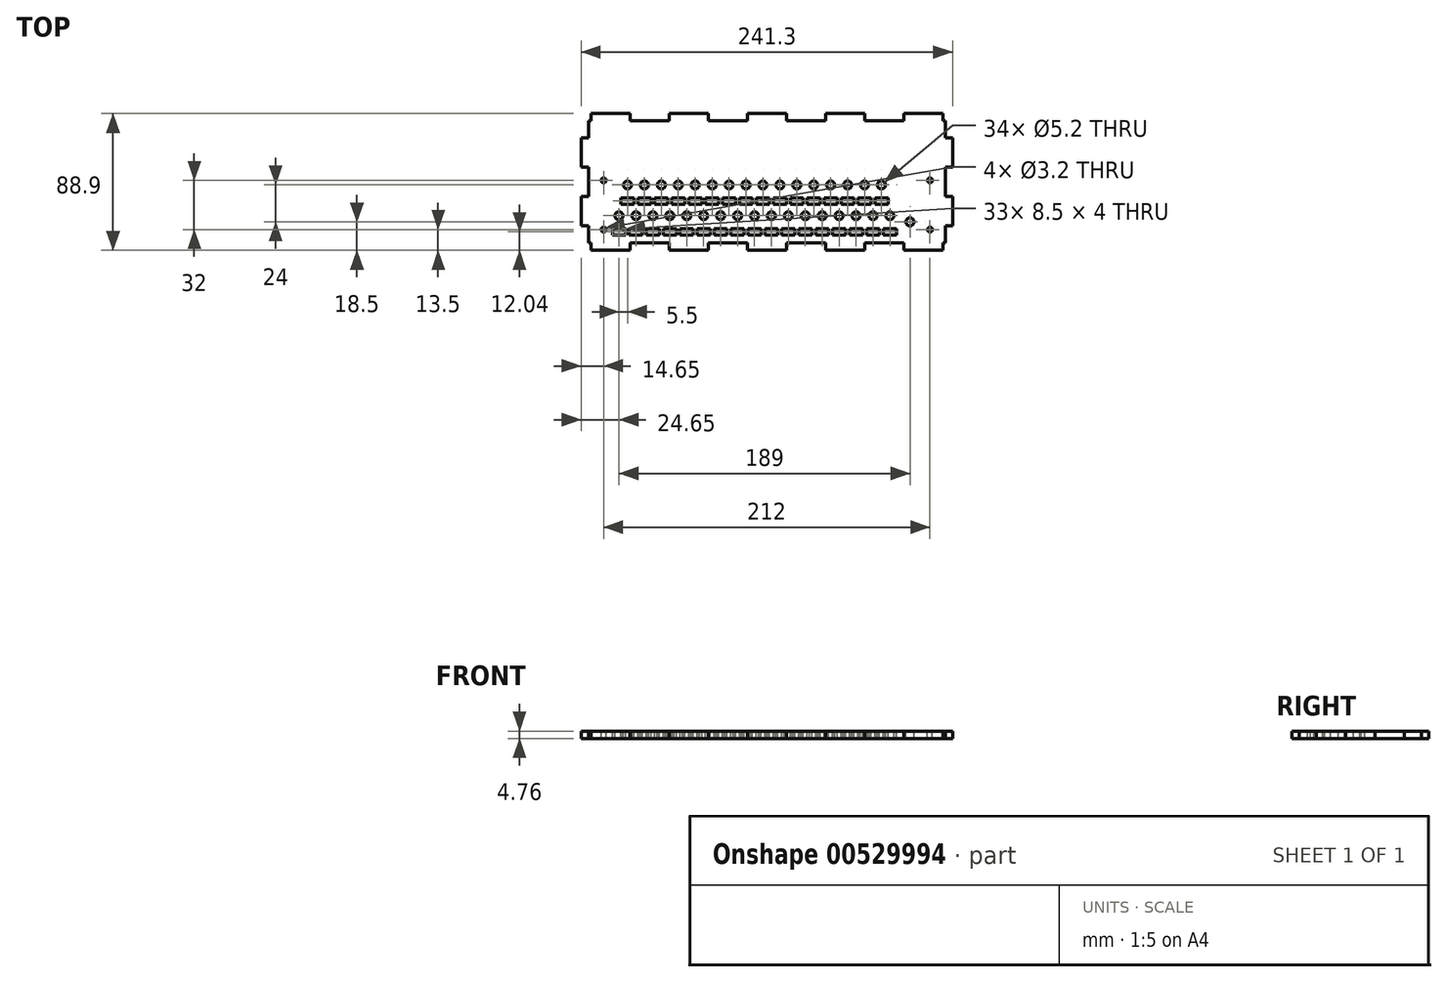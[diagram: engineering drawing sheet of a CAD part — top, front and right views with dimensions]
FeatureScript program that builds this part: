
annotation { "Feature Type Name" : "Feature", "Feature Type Description" : "" }
export const myFeature = defineFeature(function(context is Context, id is Id, definition is map)
    precondition{}
    {
        {
            var Q0;
            Q0=qCreatedBy(makeId("Top.planeOp"),FACE);
            var sketch = newSketch(context, id + "F0", { "sketchPlane" : qUnion([Q0])});
            skLineSegment(sketch, "E0.bottom", {"start": v(-120.65, 44.45) * mm, "end": v(120.65, 44.45) * mm});
            skLineSegment(sketch, "E0.top", {"start": v(-120.65, -44.45) * mm, "end": v(120.65, -44.45) * mm});
            skLineSegment(sketch, "E0.left", {"start": v(-120.65, 44.45) * mm, "end": v(-120.65, -44.45) * mm});
            skLineSegment(sketch, "E0.right", {"start": v(120.65, 44.45) * mm, "end": v(120.65, -44.45) * mm});
            skPoint(sketch, "E0.middle", {"position": v(0, 0) * mm});
            skSolve(sketch);
        }
        {
            var Q0;
            Q0 = qSketchRegion(id + "F0", true);
            extrude(context, id + "F1", {"entities" : qUnion([Q0]), "depth" : 4.76 * mm, "offsetDistance" : 25.4 * mm});
        }
        {
            var Q0;
            Q0=makeQuery(id+"F1.opExtrude","CAP_FACE",FACE,{"disambiguationData":[OSD([sQuery(id+"F0.wireOp",EDGE,"E0.bottom"),sQuery(id+"F0.wireOp",EDGE,"E0.top"),sQuery(id+"F0.wireOp",EDGE,"E0.left"),sQuery(id+"F0.wireOp",EDGE,"E0.right")])],"isStart":false});
            var sketch = newSketch(context, id + "F2", { "sketchPlane" : qUnion([Q0])});
            skLineSegment(sketch, "E1", {"start": v(0, 0) * mm, "end": v(0, -44.45) * mm, "construction": true});
            skLineSegment(sketch, "E2", {"start": v(-110, 44.45) * mm, "end": v(-110, -44.45) * mm, "construction": true});
            skCircle(sketch, "E3", {"center": v(-96, -21.95) * mm, "radius": 2.6 * mm});
            skCircle(sketch, "E4.1.0.0", {"center": v(-85, -21.95) * mm, "radius": 2.6 * mm});
            skCircle(sketch, "E4.2.0.0", {"center": v(-74, -21.95) * mm, "radius": 2.6 * mm});
            skCircle(sketch, "E4.3.0.0", {"center": v(-63, -21.95) * mm, "radius": 2.6 * mm});
            skCircle(sketch, "E4.4.0.0", {"center": v(-52, -21.95) * mm, "radius": 2.6 * mm});
            skCircle(sketch, "E4.5.0.0", {"center": v(-41, -21.95) * mm, "radius": 2.6 * mm});
            skCircle(sketch, "E4.6.0.0", {"center": v(-30, -21.95) * mm, "radius": 2.6 * mm});
            skCircle(sketch, "E4.7.0.0", {"center": v(-19, -21.95) * mm, "radius": 2.6 * mm});
            skCircle(sketch, "E4.8.0.0", {"center": v(-8, -21.95) * mm, "radius": 2.6 * mm});
            skCircle(sketch, "E4.9.0.0", {"center": v(3, -21.95) * mm, "radius": 2.6 * mm});
            skCircle(sketch, "E4.10.0.0", {"center": v(14, -21.95) * mm, "radius": 2.6 * mm});
            skCircle(sketch, "E4.11.0.0", {"center": v(25, -21.95) * mm, "radius": 2.6 * mm});
            skCircle(sketch, "E4.12.0.0", {"center": v(36, -21.95) * mm, "radius": 2.6 * mm});
            skCircle(sketch, "E4.13.0.0", {"center": v(47, -21.95) * mm, "radius": 2.6 * mm});
            skCircle(sketch, "E4.14.0.0", {"center": v(58, -21.95) * mm, "radius": 2.6 * mm});
            skCircle(sketch, "E4.15.0.0", {"center": v(69, -21.95) * mm, "radius": 2.6 * mm});
            skCircle(sketch, "E4.16.0.0", {"center": v(80, -21.95) * mm, "radius": 2.6 * mm});
            skLineSegment(sketch, "E4.direction1", {"start": v(-96, -21.95) * mm, "end": v(-85, -21.95) * mm, "construction": true});
            skCircle(sketch, "E5", {"center": v(93, -25.95) * mm, "radius": 2.6 * mm});
            skCircle(sketch, "E6", {"center": v(-90.5, -1.95) * mm, "radius": 2.6 * mm});
            skCircle(sketch, "E7.1.0.0", {"center": v(-79.5, -1.95) * mm, "radius": 2.6 * mm});
            skCircle(sketch, "E7.2.0.0", {"center": v(-68.5, -1.95) * mm, "radius": 2.6 * mm});
            skCircle(sketch, "E7.3.0.0", {"center": v(-57.5, -1.95) * mm, "radius": 2.6 * mm});
            skCircle(sketch, "E7.4.0.0", {"center": v(-46.5, -1.95) * mm, "radius": 2.6 * mm});
            skCircle(sketch, "E7.5.0.0", {"center": v(-35.5, -1.95) * mm, "radius": 2.6 * mm});
            skCircle(sketch, "E7.6.0.0", {"center": v(-24.5, -1.95) * mm, "radius": 2.6 * mm});
            skCircle(sketch, "E7.7.0.0", {"center": v(-13.5, -1.95) * mm, "radius": 2.6 * mm});
            skCircle(sketch, "E7.8.0.0", {"center": v(-2.5, -1.95) * mm, "radius": 2.6 * mm});
            skCircle(sketch, "E7.9.0.0", {"center": v(8.5, -1.95) * mm, "radius": 2.6 * mm});
            skCircle(sketch, "E7.10.0.0", {"center": v(19.5, -1.95) * mm, "radius": 2.6 * mm});
            skCircle(sketch, "E7.11.0.0", {"center": v(30.5, -1.95) * mm, "radius": 2.6 * mm});
            skCircle(sketch, "E7.12.0.0", {"center": v(41.5, -1.95) * mm, "radius": 2.6 * mm});
            skCircle(sketch, "E7.13.0.0", {"center": v(52.5, -1.95) * mm, "radius": 2.6 * mm});
            skCircle(sketch, "E7.14.0.0", {"center": v(63.5, -1.95) * mm, "radius": 2.6 * mm});
            skCircle(sketch, "E7.15.0.0", {"center": v(74.5, -1.95) * mm, "radius": 2.6 * mm});
            skLineSegment(sketch, "E7.direction1", {"start": v(-90.5, -1.95) * mm, "end": v(-79.5, -1.95) * mm, "construction": true});
            skSolve(sketch);
        }
        {
            var Q0;
            Q0 = qSketchRegion(id + "F2", true);
            extrude(context, id + "F3", {"entities" : qUnion([Q0]), "operationType" : NewBodyOperationType.REMOVE, "oppositeDirection" : true, "depth" : 25.4 * mm, "offsetDistance" : 25.4 * mm});
        }
        {
            var Q0;
            Q0=makeQuery(id+"F1.opExtrude","CAP_FACE",FACE,{"disambiguationData":[OSD([sQuery(id+"F0.wireOp",EDGE,"E0.bottom"),sQuery(id+"F0.wireOp",EDGE,"E0.top"),sQuery(id+"F0.wireOp",EDGE,"E0.left"),sQuery(id+"F0.wireOp",EDGE,"E0.right")])],"isStart":false});
            var sketch = newSketch(context, id + "F4", { "sketchPlane" : qUnion([Q0])});
            skLineSegment(sketch, "E8.bottom", {"start": v(-94.75, -10.41) * mm, "end": v(-86.25, -10.41) * mm});
            skLineSegment(sketch, "E8.top", {"start": v(-94.75, -14.41) * mm, "end": v(-86.25, -14.41) * mm});
            skLineSegment(sketch, "E8.left", {"start": v(-94.75, -10.41) * mm, "end": v(-94.75, -14.41) * mm});
            skLineSegment(sketch, "E8.right", {"start": v(-86.25, -10.41) * mm, "end": v(-86.25, -14.41) * mm});
            skLineSegment(sketch, "E9", {"start": v(-90.5, -10.41) * mm, "end": v(-90.5, -14.41) * mm, "construction": true});
            skLineSegment(sketch, "E10", {"start": v(-94.75, -12.41) * mm, "end": v(-90.5, -12.41) * mm, "construction": true});
            skLineSegment(sketch, "E11", {"start": v(-90.5, -1.95) * mm, "end": v(-90.5, -9.77) * mm, "construction": true});
            skLineSegment(sketch, "E12.1.0.0", {"start": v(-79.5, -10.41) * mm, "end": v(-79.5, -14.41) * mm, "construction": true});
            skLineSegment(sketch, "E12.1.0.1", {"start": v(-83.75, -10.41) * mm, "end": v(-75.25, -10.41) * mm});
            skLineSegment(sketch, "E12.1.0.2", {"start": v(-83.75, -10.41) * mm, "end": v(-83.75, -14.41) * mm});
            skLineSegment(sketch, "E12.1.0.3", {"start": v(-83.75, -14.41) * mm, "end": v(-75.25, -14.41) * mm});
            skLineSegment(sketch, "E12.1.0.4", {"start": v(-75.25, -10.41) * mm, "end": v(-75.25, -14.41) * mm});
            skLineSegment(sketch, "E12.2.0.0", {"start": v(-68.5, -10.41) * mm, "end": v(-68.5, -14.41) * mm, "construction": true});
            skLineSegment(sketch, "E12.2.0.1", {"start": v(-72.75, -10.41) * mm, "end": v(-64.25, -10.41) * mm});
            skLineSegment(sketch, "E12.2.0.2", {"start": v(-72.75, -10.41) * mm, "end": v(-72.75, -14.41) * mm});
            skLineSegment(sketch, "E12.2.0.3", {"start": v(-72.75, -14.41) * mm, "end": v(-64.25, -14.41) * mm});
            skLineSegment(sketch, "E12.2.0.4", {"start": v(-64.25, -10.41) * mm, "end": v(-64.25, -14.41) * mm});
            skLineSegment(sketch, "E12.3.0.0", {"start": v(-57.5, -10.41) * mm, "end": v(-57.5, -14.41) * mm, "construction": true});
            skLineSegment(sketch, "E12.3.0.1", {"start": v(-61.75, -10.41) * mm, "end": v(-53.25, -10.41) * mm});
            skLineSegment(sketch, "E12.3.0.2", {"start": v(-61.75, -10.41) * mm, "end": v(-61.75, -14.41) * mm});
            skLineSegment(sketch, "E12.3.0.3", {"start": v(-61.75, -14.41) * mm, "end": v(-53.25, -14.41) * mm});
            skLineSegment(sketch, "E12.3.0.4", {"start": v(-53.25, -10.41) * mm, "end": v(-53.25, -14.41) * mm});
            skLineSegment(sketch, "E12.4.0.0", {"start": v(-46.5, -10.41) * mm, "end": v(-46.5, -14.41) * mm, "construction": true});
            skLineSegment(sketch, "E12.4.0.1", {"start": v(-50.75, -10.41) * mm, "end": v(-42.25, -10.41) * mm});
            skLineSegment(sketch, "E12.4.0.2", {"start": v(-50.75, -10.41) * mm, "end": v(-50.75, -14.41) * mm});
            skLineSegment(sketch, "E12.4.0.3", {"start": v(-50.75, -14.41) * mm, "end": v(-42.25, -14.41) * mm});
            skLineSegment(sketch, "E12.4.0.4", {"start": v(-42.25, -10.41) * mm, "end": v(-42.25, -14.41) * mm});
            skLineSegment(sketch, "E12.5.0.0", {"start": v(-35.5, -10.41) * mm, "end": v(-35.5, -14.41) * mm, "construction": true});
            skLineSegment(sketch, "E12.5.0.1", {"start": v(-39.75, -10.41) * mm, "end": v(-31.25, -10.41) * mm});
            skLineSegment(sketch, "E12.5.0.2", {"start": v(-39.75, -10.41) * mm, "end": v(-39.75, -14.41) * mm});
            skLineSegment(sketch, "E12.5.0.3", {"start": v(-39.75, -14.41) * mm, "end": v(-31.25, -14.41) * mm});
            skLineSegment(sketch, "E12.5.0.4", {"start": v(-31.25, -10.41) * mm, "end": v(-31.25, -14.41) * mm});
            skLineSegment(sketch, "E12.6.0.0", {"start": v(-24.5, -10.41) * mm, "end": v(-24.5, -14.41) * mm, "construction": true});
            skLineSegment(sketch, "E12.6.0.1", {"start": v(-28.75, -10.41) * mm, "end": v(-20.25, -10.41) * mm});
            skLineSegment(sketch, "E12.6.0.2", {"start": v(-28.75, -10.41) * mm, "end": v(-28.75, -14.41) * mm});
            skLineSegment(sketch, "E12.6.0.3", {"start": v(-28.75, -14.41) * mm, "end": v(-20.25, -14.41) * mm});
            skLineSegment(sketch, "E12.6.0.4", {"start": v(-20.25, -10.41) * mm, "end": v(-20.25, -14.41) * mm});
            skLineSegment(sketch, "E12.7.0.0", {"start": v(-13.5, -10.41) * mm, "end": v(-13.5, -14.41) * mm, "construction": true});
            skLineSegment(sketch, "E12.7.0.1", {"start": v(-17.75, -10.41) * mm, "end": v(-9.25, -10.41) * mm});
            skLineSegment(sketch, "E12.7.0.2", {"start": v(-17.75, -10.41) * mm, "end": v(-17.75, -14.41) * mm});
            skLineSegment(sketch, "E12.7.0.3", {"start": v(-17.75, -14.41) * mm, "end": v(-9.25, -14.41) * mm});
            skLineSegment(sketch, "E12.7.0.4", {"start": v(-9.25, -10.41) * mm, "end": v(-9.25, -14.41) * mm});
            skLineSegment(sketch, "E12.8.0.0", {"start": v(-2.5, -10.41) * mm, "end": v(-2.5, -14.41) * mm, "construction": true});
            skLineSegment(sketch, "E12.8.0.1", {"start": v(-6.75, -10.41) * mm, "end": v(1.75, -10.41) * mm});
            skLineSegment(sketch, "E12.8.0.2", {"start": v(-6.75, -10.41) * mm, "end": v(-6.75, -14.41) * mm});
            skLineSegment(sketch, "E12.8.0.3", {"start": v(-6.75, -14.41) * mm, "end": v(1.75, -14.41) * mm});
            skLineSegment(sketch, "E12.8.0.4", {"start": v(1.75, -10.41) * mm, "end": v(1.75, -14.41) * mm});
            skLineSegment(sketch, "E12.9.0.0", {"start": v(8.5, -10.41) * mm, "end": v(8.5, -14.41) * mm, "construction": true});
            skLineSegment(sketch, "E12.9.0.1", {"start": v(4.25, -10.41) * mm, "end": v(12.75, -10.41) * mm});
            skLineSegment(sketch, "E12.9.0.2", {"start": v(4.25, -10.41) * mm, "end": v(4.25, -14.41) * mm});
            skLineSegment(sketch, "E12.9.0.3", {"start": v(4.25, -14.41) * mm, "end": v(12.75, -14.41) * mm});
            skLineSegment(sketch, "E12.9.0.4", {"start": v(12.75, -10.41) * mm, "end": v(12.75, -14.41) * mm});
            skLineSegment(sketch, "E12.10.0.0", {"start": v(19.5, -10.41) * mm, "end": v(19.5, -14.41) * mm, "construction": true});
            skLineSegment(sketch, "E12.10.0.1", {"start": v(15.25, -10.41) * mm, "end": v(23.75, -10.41) * mm});
            skLineSegment(sketch, "E12.10.0.2", {"start": v(15.25, -10.41) * mm, "end": v(15.25, -14.41) * mm});
            skLineSegment(sketch, "E12.10.0.3", {"start": v(15.25, -14.41) * mm, "end": v(23.75, -14.41) * mm});
            skLineSegment(sketch, "E12.10.0.4", {"start": v(23.75, -10.41) * mm, "end": v(23.75, -14.41) * mm});
            skLineSegment(sketch, "E12.11.0.0", {"start": v(30.5, -10.41) * mm, "end": v(30.5, -14.41) * mm, "construction": true});
            skLineSegment(sketch, "E12.11.0.1", {"start": v(26.25, -10.41) * mm, "end": v(34.75, -10.41) * mm});
            skLineSegment(sketch, "E12.11.0.2", {"start": v(26.25, -10.41) * mm, "end": v(26.25, -14.41) * mm});
            skLineSegment(sketch, "E12.11.0.3", {"start": v(26.25, -14.41) * mm, "end": v(34.75, -14.41) * mm});
            skLineSegment(sketch, "E12.11.0.4", {"start": v(34.75, -10.41) * mm, "end": v(34.75, -14.41) * mm});
            skLineSegment(sketch, "E12.12.0.0", {"start": v(41.5, -10.41) * mm, "end": v(41.5, -14.41) * mm, "construction": true});
            skLineSegment(sketch, "E12.12.0.1", {"start": v(37.25, -10.41) * mm, "end": v(45.75, -10.41) * mm});
            skLineSegment(sketch, "E12.12.0.2", {"start": v(37.25, -10.41) * mm, "end": v(37.25, -14.41) * mm});
            skLineSegment(sketch, "E12.12.0.3", {"start": v(37.25, -14.41) * mm, "end": v(45.75, -14.41) * mm});
            skLineSegment(sketch, "E12.12.0.4", {"start": v(45.75, -10.41) * mm, "end": v(45.75, -14.41) * mm});
            skLineSegment(sketch, "E12.13.0.0", {"start": v(52.5, -10.41) * mm, "end": v(52.5, -14.41) * mm, "construction": true});
            skLineSegment(sketch, "E12.13.0.1", {"start": v(48.25, -10.41) * mm, "end": v(56.75, -10.41) * mm});
            skLineSegment(sketch, "E12.13.0.2", {"start": v(48.25, -10.41) * mm, "end": v(48.25, -14.41) * mm});
            skLineSegment(sketch, "E12.13.0.3", {"start": v(48.25, -14.41) * mm, "end": v(56.75, -14.41) * mm});
            skLineSegment(sketch, "E12.13.0.4", {"start": v(56.75, -10.41) * mm, "end": v(56.75, -14.41) * mm});
            skLineSegment(sketch, "E12.14.0.0", {"start": v(63.5, -10.41) * mm, "end": v(63.5, -14.41) * mm, "construction": true});
            skLineSegment(sketch, "E12.14.0.1", {"start": v(59.25, -10.41) * mm, "end": v(67.75, -10.41) * mm});
            skLineSegment(sketch, "E12.14.0.2", {"start": v(59.25, -10.41) * mm, "end": v(59.25, -14.41) * mm});
            skLineSegment(sketch, "E12.14.0.3", {"start": v(59.25, -14.41) * mm, "end": v(67.75, -14.41) * mm});
            skLineSegment(sketch, "E12.14.0.4", {"start": v(67.75, -10.41) * mm, "end": v(67.75, -14.41) * mm});
            skLineSegment(sketch, "E12.15.0.0", {"start": v(74.5, -10.41) * mm, "end": v(74.5, -14.41) * mm, "construction": true});
            skLineSegment(sketch, "E12.15.0.1", {"start": v(70.25, -10.41) * mm, "end": v(78.75, -10.41) * mm});
            skLineSegment(sketch, "E12.15.0.2", {"start": v(70.25, -10.41) * mm, "end": v(70.25, -14.41) * mm});
            skLineSegment(sketch, "E12.15.0.3", {"start": v(70.25, -14.41) * mm, "end": v(78.75, -14.41) * mm});
            skLineSegment(sketch, "E12.15.0.4", {"start": v(78.75, -10.41) * mm, "end": v(78.75, -14.41) * mm});
            skLineSegment(sketch, "E12.direction1", {"start": v(-90.5, -14.41) * mm, "end": v(-79.5, -14.41) * mm, "construction": true});
            skLineSegment(sketch, "E13.bottom", {"start": v(-100.25, -30.41) * mm, "end": v(-91.75, -30.41) * mm});
            skLineSegment(sketch, "E13.top", {"start": v(-100.25, -34.41) * mm, "end": v(-91.75, -34.41) * mm});
            skLineSegment(sketch, "E13.left", {"start": v(-100.25, -30.41) * mm, "end": v(-100.25, -34.41) * mm});
            skLineSegment(sketch, "E13.right", {"start": v(-91.75, -30.41) * mm, "end": v(-91.75, -34.41) * mm});
            skLineSegment(sketch, "E14", {"start": v(-96, -30.4) * mm, "end": v(-96, -34.41) * mm, "construction": true});
            skLineSegment(sketch, "E15", {"start": v(-96, -34.41) * mm, "end": v(-96, -32.41) * mm, "construction": true});
            skLineSegment(sketch, "E16", {"start": v(-96, -32.41) * mm, "end": v(-100.25, -32.41) * mm, "construction": true});
            skLineSegment(sketch, "E17", {"start": v(-96, -21.95) * mm, "end": v(-96, -29.83) * mm, "construction": true});
            skLineSegment(sketch, "E18.1.0.0", {"start": v(-85, -34.41) * mm, "end": v(-85, -32.41) * mm, "construction": true});
            skLineSegment(sketch, "E18.1.0.1", {"start": v(-89.25, -30.41) * mm, "end": v(-89.25, -34.41) * mm});
            skLineSegment(sketch, "E18.1.0.2", {"start": v(-89.25, -30.41) * mm, "end": v(-80.75, -30.41) * mm});
            skLineSegment(sketch, "E18.1.0.3", {"start": v(-89.25, -34.41) * mm, "end": v(-80.75, -34.41) * mm});
            skLineSegment(sketch, "E18.1.0.4", {"start": v(-80.75, -30.41) * mm, "end": v(-80.75, -34.41) * mm});
            skLineSegment(sketch, "E18.2.0.0", {"start": v(-74, -34.41) * mm, "end": v(-74, -32.41) * mm, "construction": true});
            skLineSegment(sketch, "E18.2.0.1", {"start": v(-78.25, -30.41) * mm, "end": v(-78.25, -34.41) * mm});
            skLineSegment(sketch, "E18.2.0.2", {"start": v(-78.25, -30.41) * mm, "end": v(-69.75, -30.41) * mm});
            skLineSegment(sketch, "E18.2.0.3", {"start": v(-78.25, -34.41) * mm, "end": v(-69.75, -34.41) * mm});
            skLineSegment(sketch, "E18.2.0.4", {"start": v(-69.75, -30.41) * mm, "end": v(-69.75, -34.41) * mm});
            skLineSegment(sketch, "E18.3.0.0", {"start": v(-63, -34.41) * mm, "end": v(-63, -32.41) * mm, "construction": true});
            skLineSegment(sketch, "E18.3.0.1", {"start": v(-67.25, -30.41) * mm, "end": v(-67.25, -34.41) * mm});
            skLineSegment(sketch, "E18.3.0.2", {"start": v(-67.25, -30.41) * mm, "end": v(-58.75, -30.41) * mm});
            skLineSegment(sketch, "E18.3.0.3", {"start": v(-67.25, -34.41) * mm, "end": v(-58.75, -34.41) * mm});
            skLineSegment(sketch, "E18.3.0.4", {"start": v(-58.75, -30.41) * mm, "end": v(-58.75, -34.41) * mm});
            skLineSegment(sketch, "E18.4.0.0", {"start": v(-52, -34.41) * mm, "end": v(-52, -32.41) * mm, "construction": true});
            skLineSegment(sketch, "E18.4.0.1", {"start": v(-56.25, -30.41) * mm, "end": v(-56.25, -34.41) * mm});
            skLineSegment(sketch, "E18.4.0.2", {"start": v(-56.25, -30.41) * mm, "end": v(-47.75, -30.41) * mm});
            skLineSegment(sketch, "E18.4.0.3", {"start": v(-56.25, -34.41) * mm, "end": v(-47.75, -34.41) * mm});
            skLineSegment(sketch, "E18.4.0.4", {"start": v(-47.75, -30.41) * mm, "end": v(-47.75, -34.41) * mm});
            skLineSegment(sketch, "E18.5.0.0", {"start": v(-41, -34.41) * mm, "end": v(-41, -32.41) * mm, "construction": true});
            skLineSegment(sketch, "E18.5.0.1", {"start": v(-45.25, -30.41) * mm, "end": v(-45.25, -34.41) * mm});
            skLineSegment(sketch, "E18.5.0.2", {"start": v(-45.25, -30.41) * mm, "end": v(-36.75, -30.41) * mm});
            skLineSegment(sketch, "E18.5.0.3", {"start": v(-45.25, -34.41) * mm, "end": v(-36.75, -34.41) * mm});
            skLineSegment(sketch, "E18.5.0.4", {"start": v(-36.75, -30.41) * mm, "end": v(-36.75, -34.41) * mm});
            skLineSegment(sketch, "E18.6.0.0", {"start": v(-30, -34.41) * mm, "end": v(-30, -32.41) * mm, "construction": true});
            skLineSegment(sketch, "E18.6.0.1", {"start": v(-34.25, -30.41) * mm, "end": v(-34.25, -34.41) * mm});
            skLineSegment(sketch, "E18.6.0.2", {"start": v(-34.25, -30.41) * mm, "end": v(-25.75, -30.41) * mm});
            skLineSegment(sketch, "E18.6.0.3", {"start": v(-34.25, -34.41) * mm, "end": v(-25.75, -34.41) * mm});
            skLineSegment(sketch, "E18.6.0.4", {"start": v(-25.75, -30.41) * mm, "end": v(-25.75, -34.41) * mm});
            skLineSegment(sketch, "E18.7.0.0", {"start": v(-19, -34.41) * mm, "end": v(-19, -32.41) * mm, "construction": true});
            skLineSegment(sketch, "E18.7.0.1", {"start": v(-23.25, -30.41) * mm, "end": v(-23.25, -34.41) * mm});
            skLineSegment(sketch, "E18.7.0.2", {"start": v(-23.25, -30.41) * mm, "end": v(-14.75, -30.41) * mm});
            skLineSegment(sketch, "E18.7.0.3", {"start": v(-23.25, -34.41) * mm, "end": v(-14.75, -34.41) * mm});
            skLineSegment(sketch, "E18.7.0.4", {"start": v(-14.75, -30.41) * mm, "end": v(-14.75, -34.41) * mm});
            skLineSegment(sketch, "E18.8.0.0", {"start": v(-8, -34.41) * mm, "end": v(-8, -32.41) * mm, "construction": true});
            skLineSegment(sketch, "E18.8.0.1", {"start": v(-12.25, -30.41) * mm, "end": v(-12.25, -34.41) * mm});
            skLineSegment(sketch, "E18.8.0.2", {"start": v(-12.25, -30.41) * mm, "end": v(-3.75, -30.41) * mm});
            skLineSegment(sketch, "E18.8.0.3", {"start": v(-12.25, -34.41) * mm, "end": v(-3.75, -34.41) * mm});
            skLineSegment(sketch, "E18.8.0.4", {"start": v(-3.75, -30.41) * mm, "end": v(-3.75, -34.41) * mm});
            skLineSegment(sketch, "E18.9.0.0", {"start": v(3, -34.41) * mm, "end": v(3, -32.41) * mm, "construction": true});
            skLineSegment(sketch, "E18.9.0.1", {"start": v(-1.25, -30.41) * mm, "end": v(-1.25, -34.41) * mm});
            skLineSegment(sketch, "E18.9.0.2", {"start": v(-1.25, -30.41) * mm, "end": v(7.25, -30.41) * mm});
            skLineSegment(sketch, "E18.9.0.3", {"start": v(-1.25, -34.41) * mm, "end": v(7.25, -34.41) * mm});
            skLineSegment(sketch, "E18.9.0.4", {"start": v(7.25, -30.41) * mm, "end": v(7.25, -34.41) * mm});
            skLineSegment(sketch, "E18.10.0.0", {"start": v(14, -34.41) * mm, "end": v(14, -32.41) * mm, "construction": true});
            skLineSegment(sketch, "E18.10.0.1", {"start": v(9.75, -30.41) * mm, "end": v(9.75, -34.41) * mm});
            skLineSegment(sketch, "E18.10.0.2", {"start": v(9.75, -30.41) * mm, "end": v(18.25, -30.41) * mm});
            skLineSegment(sketch, "E18.10.0.3", {"start": v(9.75, -34.41) * mm, "end": v(18.25, -34.41) * mm});
            skLineSegment(sketch, "E18.10.0.4", {"start": v(18.25, -30.41) * mm, "end": v(18.25, -34.41) * mm});
            skLineSegment(sketch, "E18.11.0.0", {"start": v(25, -34.41) * mm, "end": v(25, -32.41) * mm, "construction": true});
            skLineSegment(sketch, "E18.11.0.1", {"start": v(20.75, -30.41) * mm, "end": v(20.75, -34.41) * mm});
            skLineSegment(sketch, "E18.11.0.2", {"start": v(20.75, -30.41) * mm, "end": v(29.25, -30.41) * mm});
            skLineSegment(sketch, "E18.11.0.3", {"start": v(20.75, -34.41) * mm, "end": v(29.25, -34.41) * mm});
            skLineSegment(sketch, "E18.11.0.4", {"start": v(29.25, -30.41) * mm, "end": v(29.25, -34.41) * mm});
            skLineSegment(sketch, "E18.12.0.0", {"start": v(36, -34.41) * mm, "end": v(36, -32.41) * mm, "construction": true});
            skLineSegment(sketch, "E18.12.0.1", {"start": v(31.75, -30.41) * mm, "end": v(31.75, -34.41) * mm});
            skLineSegment(sketch, "E18.12.0.2", {"start": v(31.75, -30.41) * mm, "end": v(40.25, -30.41) * mm});
            skLineSegment(sketch, "E18.12.0.3", {"start": v(31.75, -34.41) * mm, "end": v(40.25, -34.41) * mm});
            skLineSegment(sketch, "E18.12.0.4", {"start": v(40.25, -30.41) * mm, "end": v(40.25, -34.41) * mm});
            skLineSegment(sketch, "E18.13.0.0", {"start": v(47, -34.41) * mm, "end": v(47, -32.41) * mm, "construction": true});
            skLineSegment(sketch, "E18.13.0.1", {"start": v(42.75, -30.41) * mm, "end": v(42.75, -34.41) * mm});
            skLineSegment(sketch, "E18.13.0.2", {"start": v(42.75, -30.41) * mm, "end": v(51.25, -30.41) * mm});
            skLineSegment(sketch, "E18.13.0.3", {"start": v(42.75, -34.41) * mm, "end": v(51.25, -34.41) * mm});
            skLineSegment(sketch, "E18.13.0.4", {"start": v(51.25, -30.41) * mm, "end": v(51.25, -34.41) * mm});
            skLineSegment(sketch, "E18.14.0.0", {"start": v(58, -34.41) * mm, "end": v(58, -32.41) * mm, "construction": true});
            skLineSegment(sketch, "E18.14.0.1", {"start": v(53.75, -30.41) * mm, "end": v(53.75, -34.41) * mm});
            skLineSegment(sketch, "E18.14.0.2", {"start": v(53.75, -30.41) * mm, "end": v(62.25, -30.41) * mm});
            skLineSegment(sketch, "E18.14.0.3", {"start": v(53.75, -34.41) * mm, "end": v(62.25, -34.41) * mm});
            skLineSegment(sketch, "E18.14.0.4", {"start": v(62.25, -30.41) * mm, "end": v(62.25, -34.41) * mm});
            skLineSegment(sketch, "E18.15.0.0", {"start": v(69, -34.41) * mm, "end": v(69, -32.41) * mm, "construction": true});
            skLineSegment(sketch, "E18.15.0.1", {"start": v(64.75, -30.41) * mm, "end": v(64.75, -34.41) * mm});
            skLineSegment(sketch, "E18.15.0.2", {"start": v(64.75, -30.41) * mm, "end": v(73.25, -30.41) * mm});
            skLineSegment(sketch, "E18.15.0.3", {"start": v(64.75, -34.41) * mm, "end": v(73.25, -34.41) * mm});
            skLineSegment(sketch, "E18.15.0.4", {"start": v(73.25, -30.41) * mm, "end": v(73.25, -34.41) * mm});
            skLineSegment(sketch, "E18.16.0.0", {"start": v(80, -34.41) * mm, "end": v(80, -32.41) * mm, "construction": true});
            skLineSegment(sketch, "E18.16.0.1", {"start": v(75.75, -30.41) * mm, "end": v(75.75, -34.41) * mm});
            skLineSegment(sketch, "E18.16.0.2", {"start": v(75.75, -30.41) * mm, "end": v(84.25, -30.41) * mm});
            skLineSegment(sketch, "E18.16.0.3", {"start": v(75.75, -34.41) * mm, "end": v(84.25, -34.41) * mm});
            skLineSegment(sketch, "E18.16.0.4", {"start": v(84.25, -30.41) * mm, "end": v(84.25, -34.41) * mm});
            skLineSegment(sketch, "E18.direction1", {"start": v(-96, -34.41) * mm, "end": v(-85, -34.41) * mm, "construction": true});
            skSolve(sketch);
        }
        {
            var Q0;
            Q0 = qSketchRegion(id + "F4", true);
            extrude(context, id + "F5", {"entities" : qUnion([Q0]), "operationType" : NewBodyOperationType.REMOVE, "oppositeDirection" : true, "depth" : 25.4 * mm, "offsetDistance" : 25.4 * mm});
        }
        {
            var Q0;
            Q0=makeQuery(id+"F1.opExtrude","CAP_FACE",FACE,{"disambiguationData":[OSD([sQuery(id+"F0.wireOp",EDGE,"E0.bottom"),sQuery(id+"F0.wireOp",EDGE,"E0.top"),sQuery(id+"F0.wireOp",EDGE,"E0.left"),sQuery(id+"F0.wireOp",EDGE,"E0.right")])],"isStart":false});
            var sketch = newSketch(context, id + "F6", { "sketchPlane" : qUnion([Q0])});
            skLineSegment(sketch, "E19", {"start": v(0, 0) * mm, "end": v(0, 44.45) * mm, "construction": true});
            skLineSegment(sketch, "E20", {"start": v(-25.4, 44.45) * mm, "end": v(-25.4, 58.94) * mm, "construction": true});
            skLineSegment(sketch, "E21.bottom", {"start": v(-38.1, 44.45) * mm, "end": v(-12.7, 44.45) * mm});
            skLineSegment(sketch, "E21.top", {"start": v(-38.1, 39.69) * mm, "end": v(-12.7, 39.69) * mm});
            skLineSegment(sketch, "E21.left", {"start": v(-38.1, 44.45) * mm, "end": v(-38.1, 39.69) * mm});
            skLineSegment(sketch, "E21.right", {"start": v(-12.7, 44.45) * mm, "end": v(-12.7, 39.69) * mm});
            skLineSegment(sketch, "E22", {"start": v(-25.4, 39.69) * mm, "end": v(-25.4, 44.45) * mm, "construction": true});
            skLineSegment(sketch, "E23.1.0.0", {"start": v(-76.2, 39.69) * mm, "end": v(-76.2, 44.45) * mm, "construction": true});
            skLineSegment(sketch, "E23.1.0.1", {"start": v(-88.9, 44.45) * mm, "end": v(-88.9, 39.69) * mm});
            skLineSegment(sketch, "E23.1.0.2", {"start": v(-88.9, 44.45) * mm, "end": v(-63.5, 44.45) * mm});
            skLineSegment(sketch, "E23.1.0.3", {"start": v(-88.9, 39.69) * mm, "end": v(-63.5, 39.69) * mm});
            skLineSegment(sketch, "E23.1.0.4", {"start": v(-63.5, 44.45) * mm, "end": v(-63.5, 39.69) * mm});
            skLineSegment(sketch, "E23.2.0.0", {"start": v(-127, 39.69) * mm, "end": v(-127, 44.45) * mm, "construction": true});
            skLineSegment(sketch, "E23.2.0.1", {"start": v(-139.7, 44.45) * mm, "end": v(-139.7, 39.69) * mm});
            skLineSegment(sketch, "E23.2.0.2", {"start": v(-139.7, 44.45) * mm, "end": v(-114.3, 44.45) * mm});
            skLineSegment(sketch, "E23.2.0.3", {"start": v(-139.7, 39.69) * mm, "end": v(-114.3, 39.69) * mm});
            skLineSegment(sketch, "E23.2.0.4", {"start": v(-114.3, 44.45) * mm, "end": v(-114.3, 39.69) * mm});
            skLineSegment(sketch, "E23.direction1", {"start": v(-25.4, 39.69) * mm, "end": v(-76.2, 39.69) * mm, "construction": true});
            skLineSegment(sketch, "E24.MirrorCS", {"start": v(38.1, 44.45) * mm, "end": v(38.1, 39.69) * mm});
            skLineSegment(sketch, "E25.MirrorCS", {"start": v(88.9, 44.45) * mm, "end": v(88.9, 39.69) * mm});
            skLineSegment(sketch, "E26.MirrorCS", {"start": v(12.7, 44.45) * mm, "end": v(12.7, 39.69) * mm});
            skLineSegment(sketch, "E27.MirrorCS", {"start": v(25.4, 39.69) * mm, "end": v(25.4, 44.45) * mm, "construction": true});
            skLineSegment(sketch, "E28.MirrorCS", {"start": v(76.2, 39.69) * mm, "end": v(76.2, 44.45) * mm, "construction": true});
            skLineSegment(sketch, "E29.MirrorCS", {"start": v(63.5, 44.45) * mm, "end": v(63.5, 39.69) * mm});
            skLineSegment(sketch, "E30.MirrorCS", {"start": v(114.3, 44.45) * mm, "end": v(114.3, 39.69) * mm});
            skLineSegment(sketch, "E31.MirrorCS", {"start": v(139.7, 44.45) * mm, "end": v(139.7, 39.69) * mm});
            skLineSegment(sketch, "E32.MirrorCS", {"start": v(127, 39.69) * mm, "end": v(127, 44.45) * mm, "construction": true});
            skLineSegment(sketch, "E33.MirrorCS", {"start": v(38.1, 39.69) * mm, "end": v(12.7, 39.69) * mm});
            skLineSegment(sketch, "E34.MirrorCS", {"start": v(88.9, 44.45) * mm, "end": v(63.5, 44.45) * mm});
            skLineSegment(sketch, "E35.MirrorCS", {"start": v(88.9, 39.69) * mm, "end": v(63.5, 39.69) * mm});
            skLineSegment(sketch, "E36.MirrorCS", {"start": v(25.4, 39.69) * mm, "end": v(76.2, 39.69) * mm, "construction": true});
            skLineSegment(sketch, "E37.MirrorCS", {"start": v(38.1, 44.45) * mm, "end": v(12.7, 44.45) * mm});
            skLineSegment(sketch, "E38.MirrorCS", {"start": v(139.7, 44.45) * mm, "end": v(114.3, 44.45) * mm});
            skLineSegment(sketch, "E39.MirrorCS", {"start": v(139.7, 39.69) * mm, "end": v(114.3, 39.69) * mm});
            skLineSegment(sketch, "E40.MirrorCS", {"start": v(25.4, 44.45) * mm, "end": v(25.4, 58.94) * mm, "construction": true});
            skLineSegment(sketch, "E41", {"start": v(0, 0) * mm, "end": v(120.65, 0) * mm, "construction": true});
            skLineSegment(sketch, "E42.MirrorCS", {"start": v(-76.2, -39.69) * mm, "end": v(-76.2, -44.45) * mm, "construction": true});
            skLineSegment(sketch, "E43.MirrorCS", {"start": v(139.7, -44.45) * mm, "end": v(139.7, -39.69) * mm});
            skLineSegment(sketch, "E44.MirrorCS", {"start": v(-88.9, -44.45) * mm, "end": v(-88.9, -39.69) * mm});
            skLineSegment(sketch, "E45.MirrorCS", {"start": v(63.5, -44.45) * mm, "end": v(63.5, -39.69) * mm});
            skLineSegment(sketch, "E46.MirrorCS", {"start": v(-63.5, -44.45) * mm, "end": v(-63.5, -39.69) * mm});
            skLineSegment(sketch, "E47.MirrorCS", {"start": v(-38.1, -44.45) * mm, "end": v(-38.1, -39.69) * mm});
            skLineSegment(sketch, "E48.MirrorCS", {"start": v(-25.4, -39.69) * mm, "end": v(-25.4, -44.45) * mm, "construction": true});
            skLineSegment(sketch, "E49.MirrorCS", {"start": v(114.3, -44.45) * mm, "end": v(114.3, -39.69) * mm});
            skLineSegment(sketch, "E50.MirrorCS", {"start": v(38.1, -44.45) * mm, "end": v(38.1, -39.69) * mm});
            skLineSegment(sketch, "E51.MirrorCS", {"start": v(88.9, -44.45) * mm, "end": v(88.9, -39.69) * mm});
            skLineSegment(sketch, "E52.MirrorCS", {"start": v(12.7, -44.45) * mm, "end": v(12.7, -39.69) * mm});
            skLineSegment(sketch, "E53.MirrorCS", {"start": v(25.4, -39.69) * mm, "end": v(25.4, -44.45) * mm, "construction": true});
            skLineSegment(sketch, "E54.MirrorCS", {"start": v(-12.7, -44.45) * mm, "end": v(-12.7, -39.69) * mm});
            skLineSegment(sketch, "E55.MirrorCS", {"start": v(76.2, -39.69) * mm, "end": v(76.2, -44.45) * mm, "construction": true});
            skLineSegment(sketch, "E56.MirrorCS", {"start": v(-114.3, -44.45) * mm, "end": v(-114.3, -39.69) * mm});
            skLineSegment(sketch, "E57.MirrorCS", {"start": v(-139.7, -44.45) * mm, "end": v(-139.7, -39.69) * mm});
            skLineSegment(sketch, "E58.MirrorCS", {"start": v(127, -39.69) * mm, "end": v(127, -44.45) * mm, "construction": true});
            skLineSegment(sketch, "E59.MirrorCS", {"start": v(-127, -39.69) * mm, "end": v(-127, -44.45) * mm, "construction": true});
            skLineSegment(sketch, "E60.MirrorCS", {"start": v(-38.1, -44.45) * mm, "end": v(-12.7, -44.45) * mm});
            skLineSegment(sketch, "E61.MirrorCS", {"start": v(-38.1, -39.69) * mm, "end": v(-12.7, -39.69) * mm});
            skLineSegment(sketch, "E62.MirrorCS", {"start": v(88.9, -39.69) * mm, "end": v(63.5, -39.69) * mm});
            skLineSegment(sketch, "E63.MirrorCS", {"start": v(139.7, -39.69) * mm, "end": v(114.3, -39.69) * mm});
            skLineSegment(sketch, "E64.MirrorCS", {"start": v(38.1, -39.69) * mm, "end": v(12.7, -39.69) * mm});
            skLineSegment(sketch, "E65.MirrorCS", {"start": v(25.4, -39.69) * mm, "end": v(76.2, -39.69) * mm, "construction": true});
            skLineSegment(sketch, "E66.MirrorCS", {"start": v(-88.9, -44.45) * mm, "end": v(-63.5, -44.45) * mm});
            skLineSegment(sketch, "E67.MirrorCS", {"start": v(-88.9, -39.69) * mm, "end": v(-63.5, -39.69) * mm});
            skLineSegment(sketch, "E68.MirrorCS", {"start": v(-25.4, -39.69) * mm, "end": v(-76.2, -39.69) * mm, "construction": true});
            skLineSegment(sketch, "E69.MirrorCS", {"start": v(88.9, -44.45) * mm, "end": v(63.5, -44.45) * mm});
            skLineSegment(sketch, "E70.MirrorCS", {"start": v(38.1, -44.45) * mm, "end": v(12.7, -44.45) * mm});
            skLineSegment(sketch, "E71.MirrorCS", {"start": v(139.7, -44.45) * mm, "end": v(114.3, -44.45) * mm});
            skLineSegment(sketch, "E72.MirrorCS", {"start": v(-139.7, -44.45) * mm, "end": v(-114.3, -44.45) * mm});
            skLineSegment(sketch, "E73.MirrorCS", {"start": v(-139.7, -39.69) * mm, "end": v(-114.3, -39.69) * mm});
            skSolve(sketch);
        }
        {
            var Q0;
            Q0 = qSketchRegion(id + "F6", true);
            extrude(context, id + "F7", {"entities" : qUnion([Q0]), "operationType" : NewBodyOperationType.REMOVE, "oppositeDirection" : true, "depth" : 25.4 * mm, "offsetDistance" : 25.4 * mm});
        }
        {
            var Q0;
            Q0=makeQuery(id+"F1.opExtrude","CAP_FACE",FACE,{"disambiguationData":[OSD([sQuery(id+"F0.wireOp",EDGE,"E0.bottom"),sQuery(id+"F0.wireOp",EDGE,"E0.top"),sQuery(id+"F0.wireOp",EDGE,"E0.left"),sQuery(id+"F0.wireOp",EDGE,"E0.right")])],"isStart":false});
            var sketch = newSketch(context, id + "F8", { "sketchPlane" : qUnion([Q0])});
            skCircle(sketch, "E74", {"center": v(-106, -30.95) * mm, "radius": 1.6 * mm});
            skLineSegment(sketch, "E75", {"start": v(-110, 72.65) * mm, "end": v(-110, -79.26) * mm, "construction": true});
            skCircle(sketch, "E76.0", {"center": v(-96, -21.95) * mm, "radius": 2.6 * mm, "construction": true});
            skCircle(sketch, "E77.0.1.0", {"center": v(-106, 1.05) * mm, "radius": 1.6 * mm});
            skCircle(sketch, "E77.1.0.0", {"center": v(106, -30.95) * mm, "radius": 1.6 * mm});
            skCircle(sketch, "E77.1.1.0", {"center": v(106, 1.05) * mm, "radius": 1.6 * mm});
            skLineSegment(sketch, "E77.direction1", {"start": v(-106, -30.95) * mm, "end": v(106, -30.95) * mm, "construction": true});
            skLineSegment(sketch, "E77.direction2", {"start": v(-106, -30.95) * mm, "end": v(-106, 1.05) * mm, "construction": true});
            skSolve(sketch);
        }
        {
            var Q0;
            Q0 = qSketchRegion(id + "F8", true);
            extrude(context, id + "F9", {"entities" : qUnion([Q0]), "operationType" : NewBodyOperationType.REMOVE, "oppositeDirection" : true, "depth" : 25.4 * mm, "offsetDistance" : 25.4 * mm});
        }
        {
            var Q0;
            Q0=makeQuery(id+"F1.opExtrude","CAP_FACE",FACE,{"disambiguationData":[OSD([sQuery(id+"F0.wireOp",EDGE,"E0.bottom"),sQuery(id+"F0.wireOp",EDGE,"E0.top"),sQuery(id+"F0.wireOp",EDGE,"E0.left"),sQuery(id+"F0.wireOp",EDGE,"E0.right")])],"isStart":false});
            var sketch = newSketch(context, id + "F10", { "sketchPlane" : qUnion([Q0])});
            skLineSegment(sketch, "E78", {"start": v(0, 0) * mm, "end": v(-120.65, 0) * mm, "construction": true});
            skLineSegment(sketch, "E79.bottom", {"start": v(-120.65, -9.53) * mm, "end": v(-115.89, -9.53) * mm});
            skLineSegment(sketch, "E79.top", {"start": v(-120.65, 9.52) * mm, "end": v(-115.89, 9.52) * mm});
            skLineSegment(sketch, "E79.left", {"start": v(-120.65, 9.52) * mm, "end": v(-120.65, -9.52) * mm});
            skLineSegment(sketch, "E79.right", {"start": v(-115.89, 9.52) * mm, "end": v(-115.89, -9.52) * mm});
            skLineSegment(sketch, "E80", {"start": v(-120.65, 0) * mm, "end": v(-115.89, 0) * mm, "construction": true});
            skLineSegment(sketch, "E81.0.1.0", {"start": v(-120.65, 38.1) * mm, "end": v(-115.89, 38.1) * mm, "construction": true});
            skLineSegment(sketch, "E81.0.1.1", {"start": v(-120.65, 47.62) * mm, "end": v(-115.89, 47.62) * mm});
            skLineSegment(sketch, "E81.0.1.2", {"start": v(-120.65, 47.62) * mm, "end": v(-120.65, 28.58) * mm});
            skLineSegment(sketch, "E81.0.1.3", {"start": v(-120.65, 28.58) * mm, "end": v(-115.89, 28.58) * mm});
            skLineSegment(sketch, "E81.0.1.4", {"start": v(-115.89, 47.62) * mm, "end": v(-115.89, 28.58) * mm});
            skLineSegment(sketch, "E81.direction1", {"start": v(-120.65, 0) * mm, "end": v(-95.25, 0) * mm, "construction": true});
            skLineSegment(sketch, "E81.direction2", {"start": v(-120.65, 0) * mm, "end": v(-120.65, 38.1) * mm, "construction": true});
            skLineSegment(sketch, "E82.MirrorCS", {"start": v(-120.65, -47.63) * mm, "end": v(-120.65, -28.58) * mm});
            skLineSegment(sketch, "E83.MirrorCS", {"start": v(-120.65, -47.63) * mm, "end": v(-115.89, -47.63) * mm});
            skLineSegment(sketch, "E84.MirrorCS", {"start": v(-115.89, -47.63) * mm, "end": v(-115.89, -28.58) * mm});
            skLineSegment(sketch, "E85.MirrorCS", {"start": v(-120.65, -28.58) * mm, "end": v(-115.89, -28.58) * mm});
            skLineSegment(sketch, "E86", {"start": v(0, 0) * mm, "end": v(0, 44.45) * mm, "construction": true});
            skLineSegment(sketch, "E87.MirrorCS", {"start": v(120.65, 0) * mm, "end": v(115.89, 0) * mm, "construction": true});
            skLineSegment(sketch, "E88.MirrorCS", {"start": v(120.65, -47.63) * mm, "end": v(115.89, -47.63) * mm});
            skLineSegment(sketch, "E89.MirrorCS", {"start": v(120.65, -9.53) * mm, "end": v(115.89, -9.53) * mm});
            skLineSegment(sketch, "E90.MirrorCS", {"start": v(120.65, 9.52) * mm, "end": v(115.89, 9.52) * mm});
            skLineSegment(sketch, "E91.MirrorCS", {"start": v(120.65, 9.52) * mm, "end": v(120.65, -9.53) * mm});
            skLineSegment(sketch, "E92.MirrorCS", {"start": v(120.65, 38.1) * mm, "end": v(115.89, 38.1) * mm, "construction": true});
            skLineSegment(sketch, "E93.MirrorCS", {"start": v(120.65, 47.62) * mm, "end": v(115.89, 47.62) * mm});
            skLineSegment(sketch, "E94.MirrorCS", {"start": v(120.65, 47.62) * mm, "end": v(120.65, 28.57) * mm});
            skLineSegment(sketch, "E95.MirrorCS", {"start": v(120.65, 28.57) * mm, "end": v(115.89, 28.57) * mm});
            skLineSegment(sketch, "E96.MirrorCS", {"start": v(120.65, -28.58) * mm, "end": v(115.89, -28.58) * mm});
            skLineSegment(sketch, "E97.MirrorCS", {"start": v(115.89, 9.52) * mm, "end": v(115.89, -9.53) * mm});
            skLineSegment(sketch, "E98.MirrorCS", {"start": v(115.89, 47.62) * mm, "end": v(115.89, 28.57) * mm});
            skLineSegment(sketch, "E99.MirrorCS", {"start": v(120.65, -47.63) * mm, "end": v(120.65, -28.58) * mm});
            skLineSegment(sketch, "E100.MirrorCS", {"start": v(115.89, -47.63) * mm, "end": v(115.89, -28.58) * mm});
            skLineSegment(sketch, "E101.MirrorCS", {"start": v(120.65, 0) * mm, "end": v(120.65, 38.1) * mm, "construction": true});
            skSolve(sketch);
        }
        {
            var Q0;
            Q0 = qSketchRegion(id + "F10", true);
            extrude(context, id + "F11", {"entities" : qUnion([Q0]), "operationType" : NewBodyOperationType.REMOVE, "oppositeDirection" : true, "depth" : 25.4 * mm, "offsetDistance" : 25.4 * mm});
        }
    });
